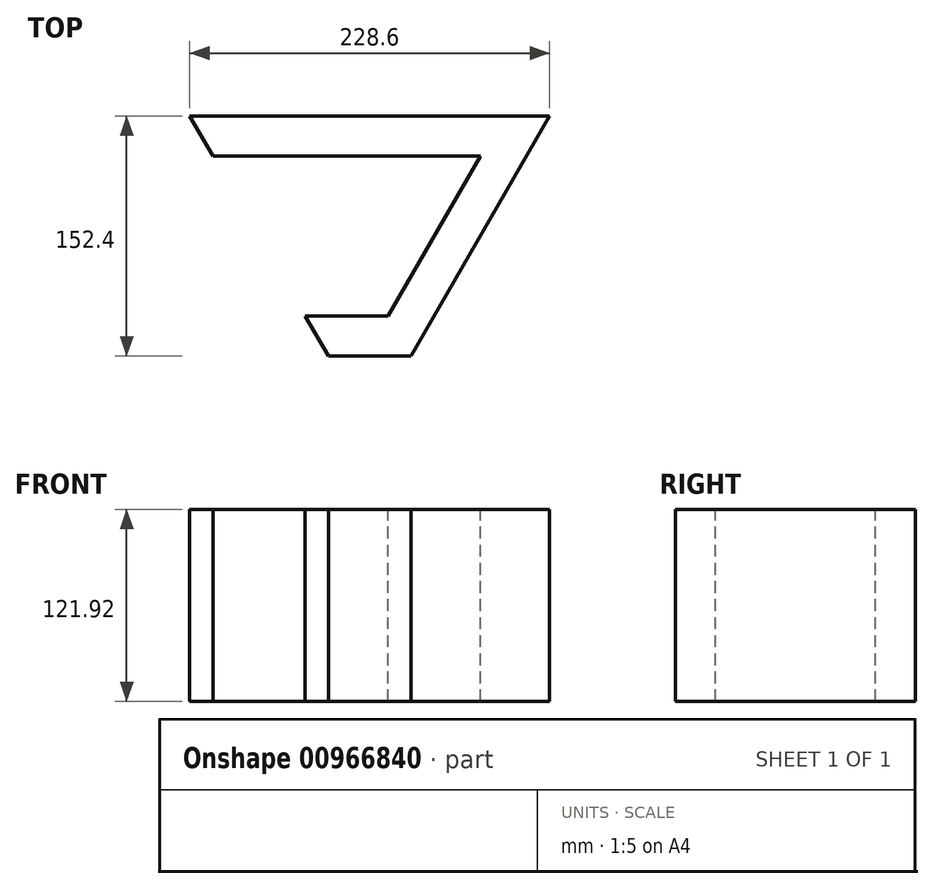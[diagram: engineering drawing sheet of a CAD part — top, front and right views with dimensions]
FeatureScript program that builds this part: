
annotation { "Feature Type Name" : "Feature", "Feature Type Description" : "" }
export const myFeature = defineFeature(function(context is Context, id is Id, definition is map)
    precondition{}
    {
        {
            var Q0;
            Q0=qCreatedBy(makeId("Top.planeOp"),FACE);
            var sketch = newSketch(context, id + "F0", { "sketchPlane" : qUnion([Q0])});
            skLineSegment(sketch, "E0.bottom", {"start": v(-101.6, 25.4) * mm, "end": v(127, 25.4) * mm});
            skLineSegment(sketch, "E0.top", {"start": v(-13.61, -127) * mm, "end": v(39.01, -127) * mm});
            skLineSegment(sketch, "E0.left", {"start": v(-101.6, 25.4) * mm, "end": v(-13.61, -127) * mm});
            skLineSegment(sketch, "E0.right", {"start": v(127, 25.4) * mm, "end": v(39.01, -127) * mm});
            skSolve(sketch);
        }
        {
            var Q0;
            Q0=makeQuery(id+"F0.imprint","IMPRINT",FACE,{"disambiguationData":[TD([[makeQuery(id+"F0.imprint","IMPRINT",EDGE,{"derivedFrom":sQuery(id+"F0.wireOp",EDGE,"E0.bottom")}),-1.0]])]});
            extrude(context, id + "F1", {"entities" : qUnion([Q0]), "oppositeDirection" : true, "depth" : 57.4 * mm, "offsetDistance" : 25.4 * mm, "hasSecondDirection" : true, "secondDirectionOppositeDirection" : false, "secondDirectionDepth" : 64.52 * mm});
        }
        {
            var Q0;
            Q0=makeQuery(id+"F1.opExtrude","CAP_FACE",FACE,{"disambiguationData":[OSD([sQuery(id+"F0.wireOp",EDGE,"E0.bottom"),sQuery(id+"F0.wireOp",EDGE,"E0.top"),sQuery(id+"F0.wireOp",EDGE,"E0.left"),sQuery(id+"F0.wireOp",EDGE,"E0.right")])],"isStart":true});
            var Q1;
            Q1=makeQuery(id+"F1.opExtrude","CAP_FACE",FACE,{"disambiguationData":[OSD([sQuery(id+"F0.wireOp",EDGE,"E0.bottom"),sQuery(id+"F0.wireOp",EDGE,"E0.top"),sQuery(id+"F0.wireOp",EDGE,"E0.left"),sQuery(id+"F0.wireOp",EDGE,"E0.right")])],"isStart":false});
            var Q2;
            Q2=makeQuery(id+"F1.opExtrude","SWEPT_FACE",FACE,{"disambiguationData":[OSD([sQuery(id+"F0.wireOp",EDGE,"E0.left")])]});
            shell(context, id + "F2", {"entities" : qUnion([Q0, Q1, Q2]), "thickness" : 25.4 * mm});
        }
    });
